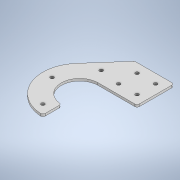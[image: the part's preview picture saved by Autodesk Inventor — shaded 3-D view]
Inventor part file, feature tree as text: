
AUTODESK INVENTOR PART (.ipt)
format: ipt  version: 2022.2 (Build 262287010, 287A)  size: 199,168 bytes
history: native  units: in
note: dims shown in document units (in); Inventor stores cm internally (conversion verified against a paired STEP export)
features: extrude x2, sketch x1, fillet x1, hole x1
ambient origin geometry x8: Origin, YZ Plane, XZ Plane, XY Plane, X Axis, Y Axis, Z Axis, Center Point
bodies: Body1 (feature_tree)
feature tree (5):
  sketch  "Sketch3"  dims[d19=1.0in d20=1.0in d21=2.125in d22=2.0in d23=2.125in d24=0.125in d25=0.0in d26=0.125in d27=0.5in d28=0.5in d29=1.0in d30=1.0in d31=1.0in d32=0.1875in d33=0.75in d34=0.375in d35=0.25in d36=0.5635in d37=1.0in d38=0.8108in d39=0.5in d40=0.1875in d42=0.5in d43=0.1875in d44=0.1875in d45=0.125in d46=0.0in]
  extrude  "Extrusion3"  Depth=1.0in
  fillet  "Fillet3"  Radius=2.125in
  hole  "Hole1"  [1 undecoded]
  extrude  "Extrusion4"  Depth=2.125in
note: 1 required parameter value undecoded (feature->parameter linkage not recoverable at this tier; creation-order binding heuristic only, values carry confidence <= 0.55)
